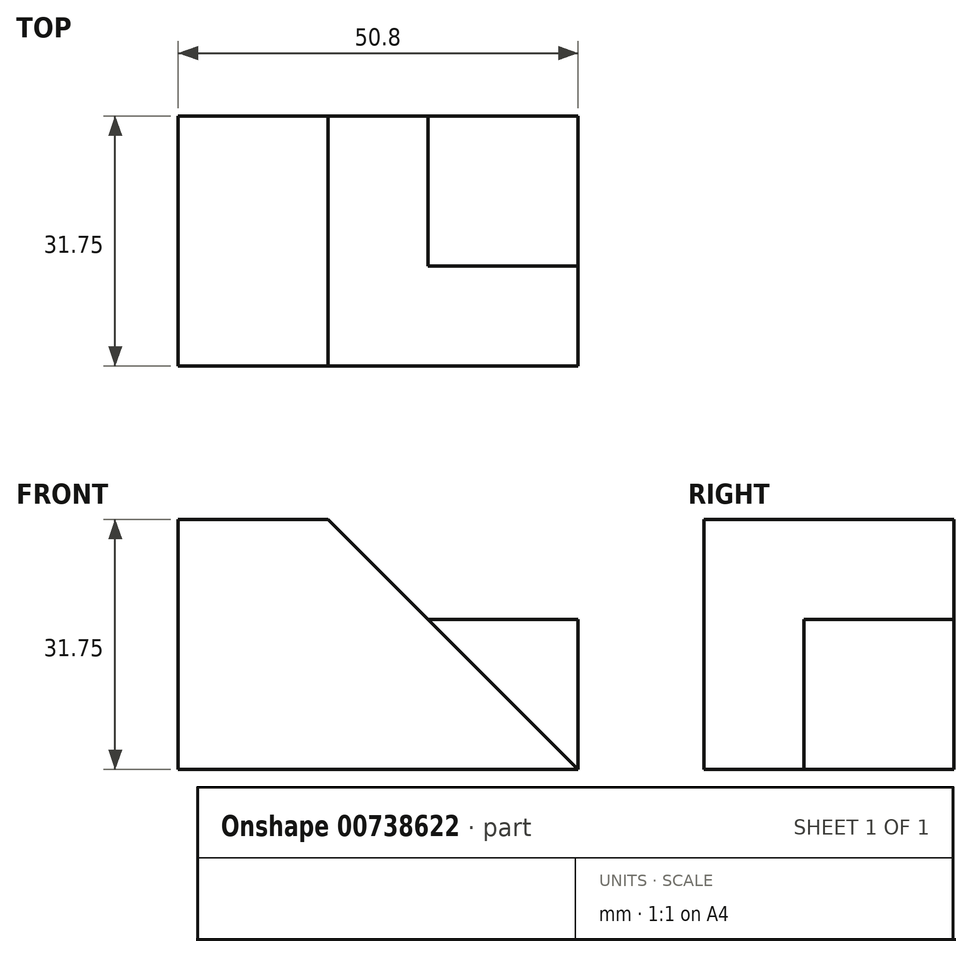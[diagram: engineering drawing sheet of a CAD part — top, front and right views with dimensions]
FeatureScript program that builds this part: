
annotation { "Feature Type Name" : "Feature", "Feature Type Description" : "" }
export const myFeature = defineFeature(function(context is Context, id is Id, definition is map)
    precondition{}
    {
        {
            var Q0;
            Q0=qCreatedBy(makeId("Top.planeOp"),FACE);
            var sketch = newSketch(context, id + "F0", { "sketchPlane" : qUnion([Q0])});
            skLineSegment(sketch, "E0.bottom", {"start": v(0, 0) * mm, "end": v(50.8, 0) * mm});
            skLineSegment(sketch, "E0.top", {"start": v(0, 31.75) * mm, "end": v(50.8, 31.75) * mm});
            skLineSegment(sketch, "E0.left", {"start": v(0, 0) * mm, "end": v(0, 31.75) * mm});
            skLineSegment(sketch, "E0.right", {"start": v(50.8, 0) * mm, "end": v(50.8, 31.75) * mm});
            skSolve(sketch);
        }
        {
            var Q0;
            Q0=makeQuery(id+"F0.imprint","IMPRINT",FACE,{"disambiguationData":[TD([[makeQuery(id+"F0.imprint","IMPRINT",EDGE,{"derivedFrom":sQuery(id+"F0.wireOp",EDGE,"E0.bottom")}),1.0]])]});
            extrude(context, id + "F1", {"entities" : qUnion([Q0]), "depth" : 31.75 * mm, "offsetDistance" : 25.4 * mm});
        }
        {
            var Q0;
            Q0=makeQuery(id+"F1.opExtrude","SWEPT_FACE",FACE,{"disambiguationData":[OSD([sQuery(id+"F0.wireOp",EDGE,"E0.bottom")])]});
            var sketch = newSketch(context, id + "F2", { "sketchPlane" : qUnion([Q0])});
            skLineSegment(sketch, "E1", {"start": v(0, 31.75) * mm, "end": v(19.05, 31.75) * mm});
            skLineSegment(sketch, "E2", {"start": v(19.05, 31.75) * mm, "end": v(50.8, 0) * mm});
            skSolve(sketch);
        }
        {
            var Q0;
            {var subQ0=sQuery(id+"F2.wireOp",EDGE,"E2");Q0=makeQuery(id+"F2.imprint","IMPRINT",FACE,{"disambiguationData":[TD([[makeQuery(id+"F2.imprint","IMPRINT",EDGE,{"derivedFrom":subQ0}),1.0]])]});}
            extrude(context, id + "F3", {"entities" : qUnion([Q0]), "operationType" : NewBodyOperationType.REMOVE, "oppositeDirection" : true, "depth" : 31.75 * mm, "offsetDistance" : 25.4 * mm});
        }
        {
            var Q0;
            Q0=makeQuery(id+"F1.opExtrude","CAP_FACE",FACE,{"disambiguationData":[OSD([sQuery(id+"F0.wireOp",EDGE,"E0.bottom"),sQuery(id+"F0.wireOp",EDGE,"E0.top"),sQuery(id+"F0.wireOp",EDGE,"E0.left"),sQuery(id+"F0.wireOp",EDGE,"E0.right")])],"isStart":true});
            var sketch = newSketch(context, id + "F4", { "sketchPlane" : qUnion([Q0])});
            skLineSegment(sketch, "E3.bottom", {"start": v(50.8, -31.75) * mm, "end": v(31.75, -31.75) * mm});
            skLineSegment(sketch, "E3.top", {"start": v(50.8, -12.7) * mm, "end": v(31.75, -12.7) * mm});
            skLineSegment(sketch, "E3.left", {"start": v(50.8, -31.75) * mm, "end": v(50.8, -12.7) * mm});
            skLineSegment(sketch, "E3.right", {"start": v(31.75, -31.75) * mm, "end": v(31.75, -12.7) * mm});
            skSolve(sketch);
        }
        {
            var Q0;
            Q0=makeQuery(id+"F4.imprint","IMPRINT",FACE,{"disambiguationData":[TD([[makeQuery(id+"F4.imprint","IMPRINT",EDGE,{"derivedFrom":sQuery(id+"F4.wireOp",EDGE,"E3.bottom")}),1.0]])]});
            extrude(context, id + "F5", {"entities" : qUnion([Q0]), "operationType" : NewBodyOperationType.ADD, "oppositeDirection" : true, "depth" : 19.05 * mm, "offsetDistance" : 25.4 * mm});
        }
    });
